# Revit family: Hager-Vector-IP65-UV_Resistance-sistema-NoHosted-ES-es
name_source: partatom
category: Electrical Equipment
units: mm (PartAtom-declared; Revit-internal decimal feet)

## family parameters
Always vertical = Yes
Cut with Voids When Loaded = No
Panel Configuration = Two Columns, Circuits Across
Part Type = Panelboard
Room Calculation Point = No
Round Connector Dimension = Use Diameter
Shared = No
Work Plane-Based = Yes

## types (10) — shared parameters
Default Elevation = 1219 mm
EF000003 - Tipo de montaje = EV000384 - Montado superficial (escayola)
EF000007 - Color = EV000270 - Gris
EF000116 - Número RAL = 7035
EF000118 - Con placa de montaje = No
EF000339 - Tipo de cubierta = EV004216 - Puerta
EF001062 - Versión de EMC = No
EF001088 - Posibilidad de extensión = Yes
EF001134 - Carril DIN = Yes
EF001596 - Material de la carcasa = EV000139 - Plástico
EF004462 - Tipo de cierre = EV000154 - Otros
EF005474 - Grado de protección (IP) = EV006421 - IP65
EF006244 - Tapa/puerta transparente = Yes
EF006306 - Con cierre = No
EF009212 - Versión de la cubierta = EV000116 - Cerrado
EF015776 - Borne de tierra = No
EF015777 - Borne neutro = No
EF015941 - Puerta de transmisión de señal = Yes
HG000001 - Número de columnas = 1
HG000002 - Con puerta o tapa = Yes
HG000003 - Gama = Vector
HG000005 - Grosor = 3 mm  [stored 0.00984252 ft]
HG000006 - Empotrado = No
HG000009 - Puerta batiente doble = No
HG000010 - Puertas asimétricas = No
HG000011 - Filas vacías desde abajo = No
HG000017 - Distancia entre polos = 18 mm  [stored 0.0590551 ft]
Manufacturer = Hager
Type Comments = Vector
zero-valued in all types: EF000218 - Profundidad de instalación, EF000332 - Altura de la instalación, EF000846 - Anchura de instalación, HG000007 - Número de columnas vacías, HG000008 - Número de filas vacías

## per-type parameters (varying)
| type | EF000008 - Anchura | EF000040 - Altura | EF000049 - Profundidad | EF000266 - Número de filas | EF001131 - Profundidad interna | EF002950 - Anchura de unidades de división | HG000004 - Referencia del fabricante | Model |
| Montado superficial IP65 A111 A175 P93 3 unidad de división - VE103SN | 111 mm | 175 mm | 93 mm | 1 | 93 mm | 3 | VE103SN | VE103SN |
| Montado superficial IP65 A165 A190 P113 6 unidad de división - VE106SN | 165 mm | 190 mm | 113 mm | 1 | 113 mm | 6 | VE106SN | VE106SN |
| Montado superficial IP65 A237 A210 P114 10 unidad de división - VE110SN | 237 mm | 210 mm | 114 mm | 1 | 114 mm | 10 | VE110SN | VE110SN |
| Montado superficial IP65 A310 A302 P151 12 unidad de división - VE112SN | 310 mm | 302 mm | 151 mm  [stored 0.495407 ft] | 1 | 151 mm  [stored 0.495407 ft] | 12 | VE112SN | VE112SN |
| Montado superficial IP65 A310 A427 P151 12 unidad de división - VE212SN | 310 mm | 427 mm | 151 mm  [stored 0.495407 ft] | 2 | 151 mm  [stored 0.495407 ft] | 12 | VE212SN | VE212SN |
| Montado superficial IP65 A310 A552 P151 12 unidad de división - VE312SN | 310 mm | 552 mm | 151 mm  [stored 0.495407 ft] | 3 | 151 mm  [stored 0.495407 ft] | 12 | VE312SN | VE312SN |
| Montado superficial IP65 A310 A677 P151 12 unidad de división - VE412SN | 310 mm | 677 mm | 151 mm  [stored 0.495407 ft] | 4 | 151 mm  [stored 0.495407 ft] | 12 | VE412SN | VE412SN |
| Montado superficial IP65 A418 A302 P151 18 unidad de división - VE118SN | 418 mm  [stored 1.37139 ft] | 302 mm | 151 mm  [stored 0.495407 ft] | 1 | 151 mm  [stored 0.495407 ft] | 18 | VE118SN | VE118SN |
| Montado superficial IP65 A418 A452 P151 18 unidad de división - VE218SN | 418 mm  [stored 1.37139 ft] | 452 mm | 151 mm  [stored 0.495407 ft] | 2 | 151 mm  [stored 0.495407 ft] | 18 | VE218SN | VE218SN |
| Montado superficial IP65 A418 A602 P151 18 unidad de división - VE318SN | 418 mm  [stored 1.37139 ft] | 602 mm  [stored 1.97507 ft] | 151 mm  [stored 0.495407 ft] | 3 | 151 mm  [stored 0.495407 ft] | 18 | VE318SN | VE318SN |

note: [stored X ft] marks values corroborated as IEEE doubles in the binary element streams (Revit-internal decimal feet)

## geometry (parser evidence)
native form markers: Sweep x13
no freeform markers — native parametric forms only
